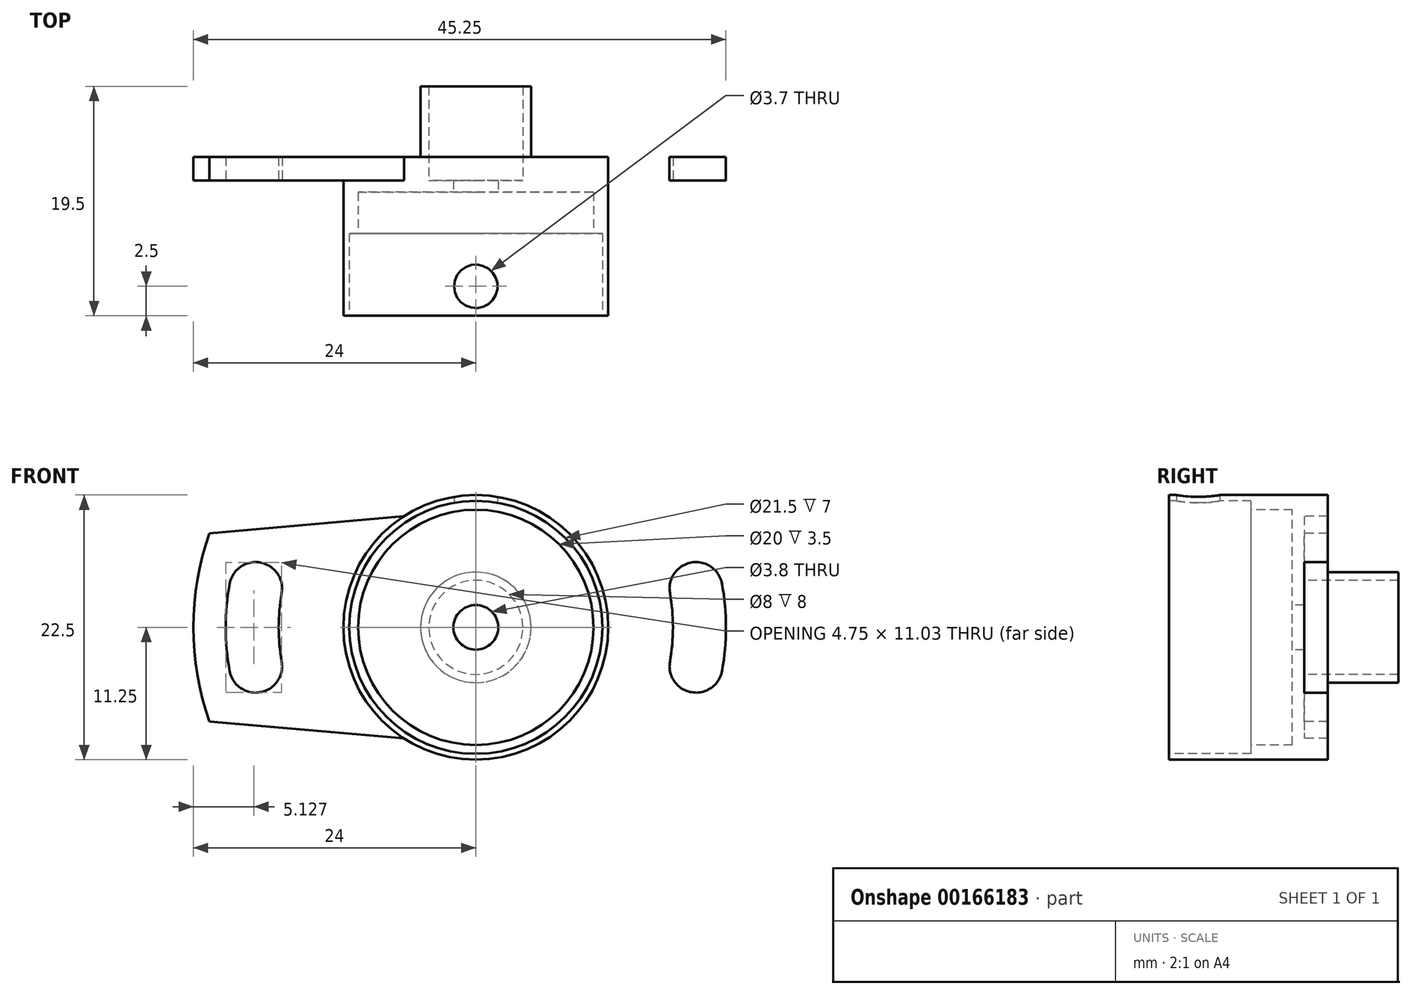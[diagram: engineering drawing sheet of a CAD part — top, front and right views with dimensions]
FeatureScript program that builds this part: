
annotation { "Feature Type Name" : "Feature", "Feature Type Description" : "" }
export const myFeature = defineFeature(function(context is Context, id is Id, definition is map)
    precondition{}
    {
        {
            var Q0;
            Q0=qCreatedBy(makeId("Right.planeOp"),FACE);
            var sketch = newSketch(context, id + "F0", { "sketchPlane" : qUnion([Q0])});
            skLineSegment(sketch, "E0", {"start": v(0, 0) * mm, "end": v(26.9, 0) * mm, "construction": true});
            skLineSegment(sketch, "E1", {"start": v(0, 11.25) * mm, "end": v(11.5, 11.25) * mm});
            skLineSegment(sketch, "E2", {"start": v(11.5, 11.25) * mm, "end": v(11.5, 4.7) * mm});
            skLineSegment(sketch, "E3", {"start": v(11.5, 4.7) * mm, "end": v(19.5, 4.7) * mm});
            skLineSegment(sketch, "E4", {"start": v(19.5, 4.7) * mm, "end": v(19.5, 4) * mm});
            skLineSegment(sketch, "E5", {"start": v(19.5, 4) * mm, "end": v(11.5, 4) * mm});
            skLineSegment(sketch, "E6", {"start": v(11.5, 4) * mm, "end": v(11.5, 1.9) * mm});
            skLineSegment(sketch, "E7", {"start": v(11.5, 1.9) * mm, "end": v(10.5, 1.9) * mm});
            skLineSegment(sketch, "E8", {"start": v(10.5, 1.9) * mm, "end": v(10.5, 10) * mm});
            skLineSegment(sketch, "E9", {"start": v(10.5, 10) * mm, "end": v(7, 10) * mm});
            skLineSegment(sketch, "E10", {"start": v(7, 10) * mm, "end": v(7, 10.75) * mm});
            skLineSegment(sketch, "E11", {"start": v(7, 10.75) * mm, "end": v(0, 10.75) * mm});
            skLineSegment(sketch, "E12", {"start": v(0, 10.75) * mm, "end": v(0, 11.25) * mm});
            skSolve(sketch);
        }
        {
            var Q0;
            Q0=makeQuery(id+"F0.imprint","IMPRINT",FACE,{"disambiguationData":[TD([[makeQuery(id+"F0.imprint","IMPRINT",EDGE,{"derivedFrom":sQuery(id+"F0.wireOp",EDGE,"E1")}),-1.0]])]});
            var Q1;
            Q1=sQuery(id+"F0.wireOp",EDGE,"E0");
            revolve(context, id + "F1", {"entities" : qUnion([Q0]), "axis" : qUnion([Q1]), "revolveType" : RevolveType.FULL});
        }
        {
            var Q0;
            Q0=qCreatedBy(makeId("Top.planeOp"),FACE);
            var sketch = newSketch(context, id + "F2", { "sketchPlane" : qUnion([Q0])});
            skCircle(sketch, "E13", {"center": v(0, 2.5) * mm, "radius": 1.85 * mm});
            skSolve(sketch);
        }
        {
            var Q0;
            Q0=makeQuery(id+"F2.imprint","IMPRINT",FACE,{"disambiguationData":[TD([[makeQuery(id+"F2.imprint","IMPRINT",EDGE,{"derivedFrom":sQuery(id+"F2.wireOp",EDGE,"E13")}),1.0]])]});
            extrude(context, id + "F3", {"entities" : qUnion([Q0]), "operationType" : NewBodyOperationType.REMOVE, "endBound" : BoundingType.THROUGH_ALL, "depth" : 25 * mm});
        }
        {
            var Q0;
            Q0=makeQuery(id+"F1.opRevolve","SWEPT_FACE",FACE,{"disambiguationData":[OSD([sQuery(id+"F0.wireOp",EDGE,"E2")])]});
            var sketch = newSketch(context, id + "F4", { "sketchPlane" : qUnion([Q0])});
            skCircle(sketch, "E14", {"center": v(0, 0) * mm, "radius": 24 * mm});
            skLineSegment(sketch, "E15", {"start": v(6.11, 9.44) * mm, "end": v(22.63, 8) * mm});
            skLineSegment(sketch, "E16", {"start": v(22.63, -8) * mm, "end": v(6.11, -9.44) * mm});
            skLineSegment(sketch, "E17", {"start": v(24, 0) * mm, "end": v(0, 0) * mm, "construction": true});
            skCircle(sketch, "E18", {"center": v(0, 0) * mm, "radius": 19 * mm, "construction": true});
            skCircle(sketch, "E19.0", {"center": v(0, 0) * mm, "radius": 11.25 * mm});
            skCircle(sketch, "E20.0", {"center": v(0, 0) * mm, "radius": 4.7 * mm});
            skArc(sketch, "E21", {"start": v(20.93, 3.7) * mm, "mid": v(18.32, 5.52) * mm, "end": v(16.5, 2.9) * mm});
            skArc(sketch, "E22", {"start": v(16.5, -2.9) * mm, "mid": v(18.32, -5.52) * mm, "end": v(20.93, -3.7) * mm});
            skLineSegment(sketch, "E23", {"start": v(0, 0) * mm, "end": v(18.71, 3.3) * mm, "construction": true});
            skLineSegment(sketch, "E24", {"start": v(0, 0) * mm, "end": v(18.71, -3.3) * mm, "construction": true});
            skArc(sketch, "E25", {"start": v(16.5, -2.9) * mm, "mid": v(16.75, 0) * mm, "end": v(16.5, 2.9) * mm});
            skArc(sketch, "E26", {"start": v(20.93, -3.7) * mm, "mid": v(21.25, 0) * mm, "end": v(20.93, 3.7) * mm});
            skLineSegment(sketch, "E27", {"start": v(0, 0) * mm, "end": v(0, 24) * mm, "construction": true});
            skArc(sketch, "E28.MirrorCS", {"start": v(-20.93, -3.7) * mm, "mid": v(-21.25, 0) * mm, "end": v(-20.93, 3.7) * mm});
            skArc(sketch, "E29.MirrorCS", {"start": v(-16.5, -2.9) * mm, "mid": v(-18.32, -5.52) * mm, "end": v(-20.93, -3.7) * mm});
            skArc(sketch, "E30.MirrorCS", {"start": v(-16.5, -2.9) * mm, "mid": v(-16.75, 0) * mm, "end": v(-16.5, 2.9) * mm});
            skArc(sketch, "E31.MirrorCS", {"start": v(-20.93, 3.7) * mm, "mid": v(-18.32, 5.52) * mm, "end": v(-16.5, 2.9) * mm});
            skLineSegment(sketch, "E32.MirrorCS", {"start": v(-6.11, 9.44) * mm, "end": v(-22.63, 8) * mm});
            skLineSegment(sketch, "E33.MirrorCS", {"start": v(-22.63, -8) * mm, "end": v(-6.11, -9.44) * mm});
            skSolve(sketch);
        }
        {
            var Q0;
            Q0=makeQuery(id+"F4.imprint","IMPRINT",FACE,{"disambiguationData":[TD([[makeQuery(id+"F4.imprint","IMPRINT",EDGE,{"derivedFrom":sQuery(id+"F4.wireOp",EDGE,"E28.MirrorCS")}),1.0]])]});
            var Q1;
            {var subQ1=sQuery(id+"F4.wireOp",EDGE,"E15");Q1=makeQuery(id+"F4.imprint","IMPRINT",FACE,{"disambiguationData":[TD([[makeQuery(id+"F4.imprint","IMPRINT",EDGE,{"derivedFrom":subQ1}),-1.0]])]});}
            var Q2;
            Q2=makeQuery(id+"F4.imprint","IMPRINT",FACE,{"disambiguationData":[TD([[makeQuery(id+"F4.imprint","IMPRINT",EDGE,{"derivedFrom":sQuery(id+"F4.wireOp",EDGE,"E20.0")}),1.0]])]});
            extrude(context, id + "F5", {"entities" : qUnion([Q0, Q1, Q2]), "operationType" : NewBodyOperationType.ADD, "depth" : 2 * mm});
        }
    });
